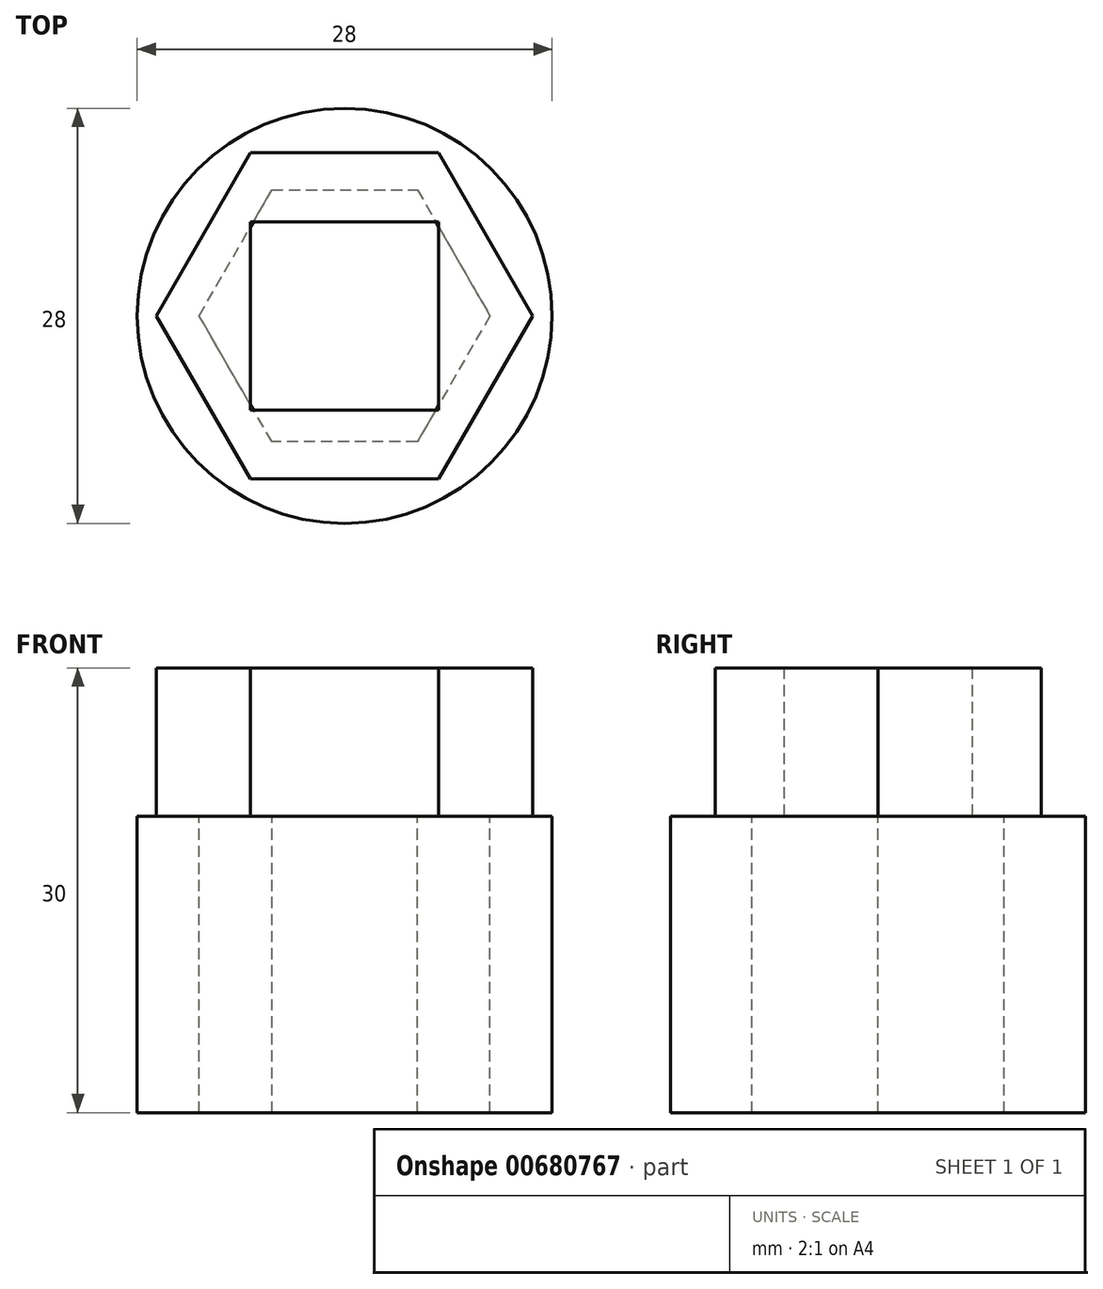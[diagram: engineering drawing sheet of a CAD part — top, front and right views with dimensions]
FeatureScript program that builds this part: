
annotation { "Feature Type Name" : "Feature", "Feature Type Description" : "" }
export const myFeature = defineFeature(function(context is Context, id is Id, definition is map)
    precondition{}
    {
        {
            assignVariable(context, id + "F0", {"name" : "length", "anyValue" : 20});
        }
        {
            var Q0;
            Q0=qCreatedBy(makeId("Top.planeOp"),FACE);
            var sketch = newSketch(context, id + "F1", { "sketchPlane" : qUnion([Q0])});
            skLineSegment(sketch, "E0", {"start": v(0, 0) * mm, "end": v(14.5, 25.1) * mm, "construction": true});
            skLineSegment(sketch, "E1", {"start": v(0, 0) * mm, "end": v(-14.5, -25.1) * mm, "construction": true});
            skLineSegment(sketch, "E2", {"start": v(0, 0) * mm, "end": v(-14.5, 25.1) * mm, "construction": true});
            skLineSegment(sketch, "E3", {"start": v(0, 0) * mm, "end": v(14.5, -25.1) * mm, "construction": true});
            skLineSegment(sketch, "E4", {"start": v(-6.35, 11) * mm, "end": v(6.35, 11) * mm});
            skLineSegment(sketch, "E5", {"start": v(6.35, 11) * mm, "end": v(12.7, 0) * mm});
            skLineSegment(sketch, "E6", {"start": v(12.7, 0) * mm, "end": v(6.35, -11) * mm});
            skLineSegment(sketch, "E7", {"start": v(6.35, -11) * mm, "end": v(-6.35, -11) * mm});
            skLineSegment(sketch, "E8", {"start": v(-6.35, -11) * mm, "end": v(-12.7, 0) * mm});
            skLineSegment(sketch, "E9", {"start": v(-12.7, 0) * mm, "end": v(-6.35, 11) * mm});
            skLineSegment(sketch, "E10.bottom", {"start": v(-6.35, 6.35) * mm, "end": v(6.35, 6.35) * mm});
            skLineSegment(sketch, "E10.top", {"start": v(-6.35, -6.35) * mm, "end": v(6.35, -6.35) * mm});
            skLineSegment(sketch, "E10.left", {"start": v(-6.35, 6.35) * mm, "end": v(-6.35, -6.35) * mm});
            skLineSegment(sketch, "E10.right", {"start": v(6.35, 6.35) * mm, "end": v(6.35, -6.35) * mm});
            skPoint(sketch, "E10.middle", {"position": v(0, 0) * mm});
            skCircle(sketch, "E11", {"center": v(0, 0) * mm, "radius": 14 * mm});
            skSolve(sketch);
        }
        {
            var Q0;
            Q0=makeQuery(id+"F1.imprint","IMPRINT",FACE,{"disambiguationData":[TD([[makeQuery(id+"F1.imprint","IMPRINT",EDGE,{"derivedFrom":sQuery(id+"F1.wireOp",EDGE,"E10.bottom")}),1.0]])]});
            extrude(context, id + "F2", {"entities" : qUnion([Q0]), "depth" : (getVariable(context, 'length') / 2) * mm, "offsetDistance" : 25 * mm});
        }
        {
            var Q0;
            Q0=qCreatedBy(makeId("Top.planeOp"),FACE);
            var sketch = newSketch(context, id + "F3", { "sketchPlane" : qUnion([Q0])});
            skLineSegment(sketch, "E12", {"start": v(0, 0) * mm, "end": v(56.14, 97.24) * mm, "construction": true});
            skLineSegment(sketch, "E13", {"start": v(0, 0) * mm, "end": v(-56.14, -97.24) * mm, "construction": true});
            skLineSegment(sketch, "E14", {"start": v(0, 0) * mm, "end": v(-56.14, 97.24) * mm, "construction": true});
            skLineSegment(sketch, "E15", {"start": v(0, 0) * mm, "end": v(56.14, -97.24) * mm, "construction": true});
            skLineSegment(sketch, "E16", {"start": v(-4.9, 8.5) * mm, "end": v(4.9, 8.5) * mm});
            skLineSegment(sketch, "E17", {"start": v(4.9, 8.5) * mm, "end": v(9.81, 0) * mm});
            skLineSegment(sketch, "E18", {"start": v(9.81, 0) * mm, "end": v(4.9, -8.5) * mm});
            skLineSegment(sketch, "E19", {"start": v(4.9, -8.5) * mm, "end": v(-4.9, -8.5) * mm});
            skLineSegment(sketch, "E20", {"start": v(-4.9, -8.5) * mm, "end": v(-9.81, 0) * mm});
            skLineSegment(sketch, "E21", {"start": v(-9.81, 0) * mm, "end": v(-4.9, 8.5) * mm});
            skCircle(sketch, "E22", {"center": v(0, 0) * mm, "radius": 14 * mm});
            skSolve(sketch);
        }
        {
            var Q0;
            Q0=makeQuery(id+"F3.imprint","IMPRINT",FACE,{"disambiguationData":[TD([[makeQuery(id+"F3.imprint","IMPRINT",EDGE,{"derivedFrom":sQuery(id+"F3.wireOp",EDGE,"E16")}),1.0]])]});
            extrude(context, id + "F4", {"entities" : qUnion([Q0]), "depth" : (-getVariable(context, 'length')) * mm, "offsetDistance" : 25 * mm});
        }
    });
